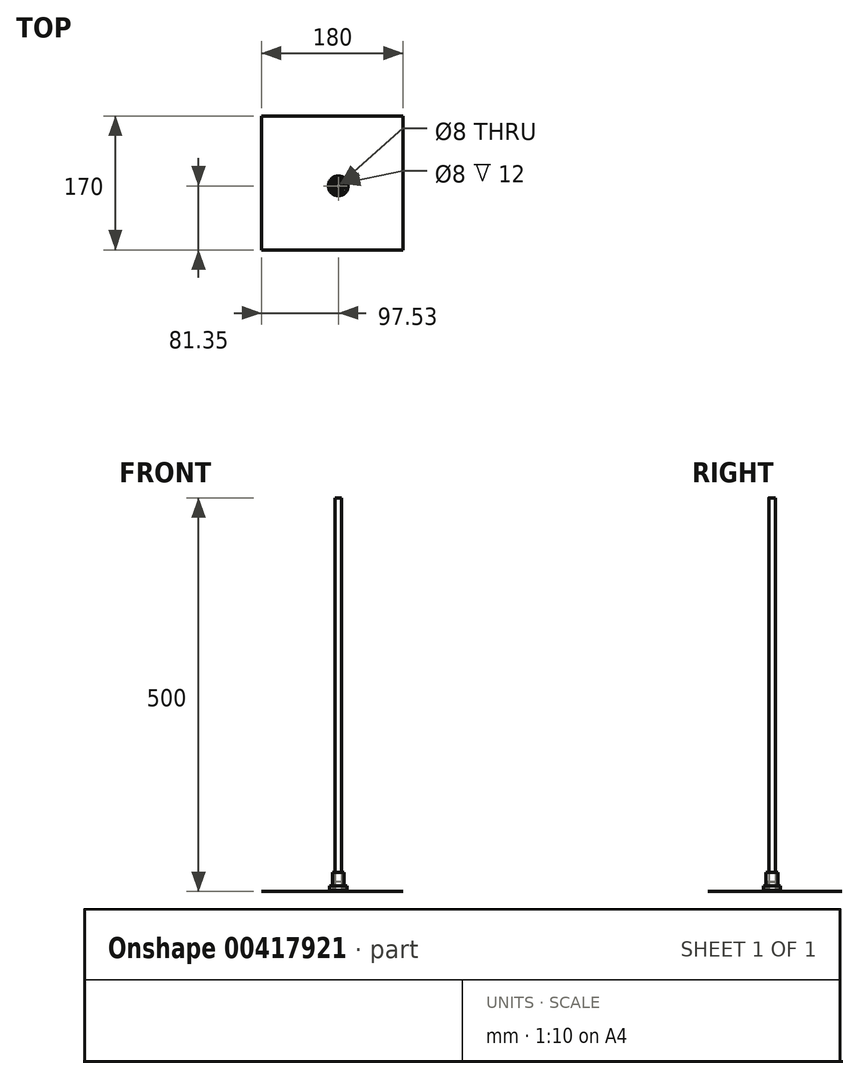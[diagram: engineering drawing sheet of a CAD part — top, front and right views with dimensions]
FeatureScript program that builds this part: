
annotation { "Feature Type Name" : "Feature", "Feature Type Description" : "" }
export const myFeature = defineFeature(function(context is Context, id is Id, definition is map)
    precondition{}
    {
        {
            var Q0;
            Q0=qCreatedBy(makeId("Top.planeOp"),FACE);
            var sketch = newSketch(context, id + "F0", { "sketchPlane" : qUnion([Q0])});
            skCircle(sketch, "E0", {"center": v(0, 0) * mm, "radius": 12.5 * mm});
            skCircle(sketch, "E1", {"center": v(0, 0) * mm, "radius": 11 * mm});
            skCircle(sketch, "E2", {"center": v(0, 0) * mm, "radius": 4 * mm});
            skSolve(sketch);
        }
        {
            var Q0;
            Q0=makeQuery(id+"F0.imprint","IMPRINT",FACE,{"disambiguationData":[TD([[makeQuery(id+"F0.imprint","IMPRINT",EDGE,{"derivedFrom":sQuery(id+"F0.wireOp",EDGE,"E1")}),1.0]])]});
            extrude(context, id + "F1", {"entities" : qUnion([Q0]), "depth" : 7 * mm});
        }
        {
            var Q0;
            Q0=makeQuery(id+"F0.imprint","IMPRINT",FACE,{"disambiguationData":[TD([[makeQuery(id+"F0.imprint","IMPRINT",EDGE,{"derivedFrom":sQuery(id+"F0.wireOp",EDGE,"E0")}),1.0]])]});
            extrude(context, id + "F2", {"entities" : qUnion([Q0]), "operationType" : NewBodyOperationType.ADD, "depth" : 1.5 * mm});
        }
        {
            var Q0;
            Q0=qCreatedBy(makeId("Top.planeOp"),FACE);
            var sketch = newSketch(context, id + "F3", { "sketchPlane" : qUnion([Q0])});
            skCircle(sketch, "E3", {"center": v(0, 0) * mm, "radius": 2 * mm});
            skCircle(sketch, "E4", {"center": v(0, 0) * mm, "radius": 6.5 * mm});
            skCircle(sketch, "E5", {"center": v(0, 0) * mm, "radius": 7.5 * mm});
            skSolve(sketch);
        }
        {
            var Q0;
            Q0=makeQuery(id+"F3.imprint","IMPRINT",FACE,{"disambiguationData":[TD([[makeQuery(id+"F3.imprint","IMPRINT",EDGE,{"derivedFrom":sQuery(id+"F3.wireOp",EDGE,"E3")}),-1.0]])]});
            extrude(context, id + "F4", {"entities" : qUnion([Q0]), "depth" : 5 * mm});
        }
        {
            var Q0;
            Q0=makeQuery(id+"F3.imprint","IMPRINT",FACE,{"disambiguationData":[TD([[makeQuery(id+"F3.imprint","IMPRINT",EDGE,{"derivedFrom":sQuery(id+"F3.wireOp",EDGE,"E4")}),-1.0]])]});
            extrude(context, id + "F5", {"entities" : qUnion([Q0]), "operationType" : NewBodyOperationType.ADD, "depth" : 1 * mm});
        }
        {
            var Q0;
            Q0=qCreatedBy(makeId("Top.planeOp"),FACE);
            var sketch = newSketch(context, id + "F6", { "sketchPlane" : qUnion([Q0])});
            skCircle(sketch, "E6", {"center": v(0, 0) * mm, "radius": 4 * mm});
            skCircle(sketch, "E7", {"center": v(0, 0) * mm, "radius": 5 * mm});
            skSolve(sketch);
        }
        {
            var Q0;
            Q0=qSketchRegion(id+"F6",true);
            var Q1;
            Q1=makeQuery(id+"F6.imprint","IMPRINT",FACE,{"disambiguationData":[TD([[makeQuery(id+"F6.imprint","IMPRINT",EDGE,{"derivedFrom":sQuery(id+"F6.wireOp",EDGE,"E6")}),-1.0]])]});
            extrude(context, id + "F7", {"entities" : qUnion([Q0, Q1]), "depth" : 12 * mm});
        }
        {
            var Q0;
            Q0=qCreatedBy(makeId("Top.planeOp"),FACE);
            var sketch = newSketch(context, id + "F8", { "sketchPlane" : qUnion([Q0])});
            skCircle(sketch, "E8", {"center": v(0, 0) * mm, "radius": 4 * mm});
            skSolve(sketch);
        }
        {
            var Q0;
            Q0=qSketchRegion(id+"F8",true);
            extrude(context, id + "F9", {"entities" : qUnion([Q0]), "depth" : 500 * mm});
        }
        {
            var Q0;
            Q0=makeQuery(id+"F8.imprint","IMPRINT",FACE,{"disambiguationData":[TD([[makeQuery(id+"F8.imprint","IMPRINT",EDGE,{"derivedFrom":sQuery(id+"F8.wireOp",EDGE,"E8")}),1.0]])]});
            var Q1;
            Q1=sQuery(id+"F8.wireOp",EDGE,"E8");
            extrude(context, id + "F10", {"entities" : qUnion([Q0]), "surfaceEntities" : qUnion([Q1]), "depth" : 200 * mm});
        }
        {
            var Q0;
            Q0=qCreatedBy(makeId("Top.planeOp"),FACE);
            var sketch = newSketch(context, id + "F11", { "sketchPlane" : qUnion([Q0])});
            skCircle(sketch, "E9.cCircle", {"center": v(0, 0) * mm, "radius": 3.9 * mm, "construction": true});
            skLineSegment(sketch, "E9.0", {"start": v(2.25, -3.9) * mm, "end": v(-2.25, -3.9) * mm});
            skLineSegment(sketch, "E9.1", {"start": v(-2.25, -3.9) * mm, "end": v(-4.5, 0) * mm});
            skLineSegment(sketch, "E9.2", {"start": v(-4.5, 0) * mm, "end": v(-2.25, 3.9) * mm});
            skLineSegment(sketch, "E9.3", {"start": v(-2.25, 3.9) * mm, "end": v(2.25, 3.9) * mm});
            skLineSegment(sketch, "E9.4", {"start": v(2.25, 3.9) * mm, "end": v(4.5, 0) * mm});
            skLineSegment(sketch, "E9.5", {"start": v(4.5, 0) * mm, "end": v(2.25, -3.9) * mm});
            skPoint(sketch, "E9.0.midPoint", {"position": v(0, -3.9) * mm});
            skSolve(sketch);
        }
        {
            var Q0;
            Q0=qSketchRegion(id+"F11",true);
            var Q1;
            Q1=makeQuery(id+"F11.imprint","IMPRINT",FACE,{"disambiguationData":[TD([[makeQuery(id+"F11.imprint","IMPRINT",EDGE,{"derivedFrom":sQuery(id+"F11.wireOp",EDGE,"E9.0")}),-1.0]])]});
            extrude(context, id + "F12", {"entities" : qUnion([Q0, Q1]), "depth" : 4 * mm});
        }
        {
            var Q0;
            Q0=makeQuery(id+"F12.opExtrude","CAP_FACE",FACE,{"disambiguationData":[OSD([sQuery(id+"F11.wireOp",EDGE,"E9.0"),sQuery(id+"F11.wireOp",EDGE,"E9.1"),sQuery(id+"F11.wireOp",EDGE,"E9.2"),sQuery(id+"F11.wireOp",EDGE,"E9.3"),sQuery(id+"F11.wireOp",EDGE,"E9.4"),sQuery(id+"F11.wireOp",EDGE,"E9.5")])],"isStart":false});
            var sketch = newSketch(context, id + "F13", { "sketchPlane" : qUnion([Q0])});
            skCircle(sketch, "E10", {"center": v(0, 0) * mm, "radius": 2.5 * mm});
            skSolve(sketch);
        }
        {
            var Q0;
            Q0=qSketchRegion(id+"F13",true);
            var Q1;
            Q1=makeQuery(id+"F13.imprint","IMPRINT",FACE,{"disambiguationData":[TD([[makeQuery(id+"F13.imprint","IMPRINT",EDGE,{"derivedFrom":sQuery(id+"F13.wireOp",EDGE,"E10")}),1.0]])]});
            extrude(context, id + "F14", {"entities" : qUnion([Q0, Q1]), "operationType" : NewBodyOperationType.ADD, "depth" : 25 * mm});
        }
        {
            var Q0;
            Q0=qCreatedBy(makeId("Top.planeOp"),FACE);
            var sketch = newSketch(context, id + "F15", { "sketchPlane" : qUnion([Q0])});
            skCircle(sketch, "E11", {"center": v(0, 0) * mm, "radius": 2.75 * mm});
            skSolve(sketch);
        }
        {
            var Q0;
            Q0=qSketchRegion(id+"F15",true);
            extrude(context, id + "F16", {"entities" : qUnion([Q0]), "depth" : 3 * mm});
        }
        {
            var Q0;
            Q0=makeQuery(id+"F16.opExtrude","CAP_FACE",FACE,{"disambiguationData":[OSD([sQuery(id+"F15.wireOp",EDGE,"E11")])],"isStart":false});
            var sketch = newSketch(context, id + "F17", { "sketchPlane" : qUnion([Q0])});
            skCircle(sketch, "E12", {"center": v(0, 0) * mm, "radius": 1.5 * mm});
            skSolve(sketch);
        }
        {
            var Q0;
            Q0=qSketchRegion(id+"F17",true);
            extrude(context, id + "F18", {"entities" : qUnion([Q0]), "operationType" : NewBodyOperationType.ADD, "depth" : 20 * mm});
        }
        {
            var Q0;
            Q0=qCreatedBy(makeId("Top.planeOp"),FACE);
            var sketch = newSketch(context, id + "F19", { "sketchPlane" : qUnion([Q0])});
            skCircle(sketch, "E13", {"center": v(0, 0) * mm, "radius": 4 * mm});
            skCircle(sketch, "E14", {"center": v(0, 0) * mm, "radius": 7.5 * mm});
            skSolve(sketch);
        }
        {
            var Q0;
            Q0=makeQuery(id+"F19.imprint","IMPRINT",FACE,{"disambiguationData":[TD([[makeQuery(id+"F19.imprint","IMPRINT",EDGE,{"derivedFrom":sQuery(id+"F19.wireOp",EDGE,"E13")}),-1.0]])]});
            extrude(context, id + "F20", {"entities" : qUnion([Q0]), "depth" : 24 * mm});
        }
        {
            var Q0;
            Q0=qCreatedBy(makeId("Top.planeOp"),FACE);
            var sketch = newSketch(context, id + "F21", { "sketchPlane" : qUnion([Q0])});
            skLineSegment(sketch, "E15.bottom", {"start": v(-97.53, 88.65) * mm, "end": v(82.47, 88.65) * mm});
            skLineSegment(sketch, "E15.top", {"start": v(-97.53, -81.35) * mm, "end": v(82.47, -81.35) * mm});
            skLineSegment(sketch, "E15.left", {"start": v(-97.53, 88.65) * mm, "end": v(-97.53, -81.35) * mm});
            skLineSegment(sketch, "E15.right", {"start": v(82.47, 88.65) * mm, "end": v(82.47, -81.35) * mm});
            skSolve(sketch);
        }
        {
            var Q0;
            Q0=makeQuery(id+"F21.imprint","IMPRINT",FACE,{"disambiguationData":[TD([[makeQuery(id+"F21.imprint","IMPRINT",EDGE,{"derivedFrom":sQuery(id+"F21.wireOp",EDGE,"E15.bottom")}),-1.0]])]});
            extrude(context, id + "F22", {"entities" : qUnion([Q0]), "depth" : 0.1 * mm});
        }
    });
